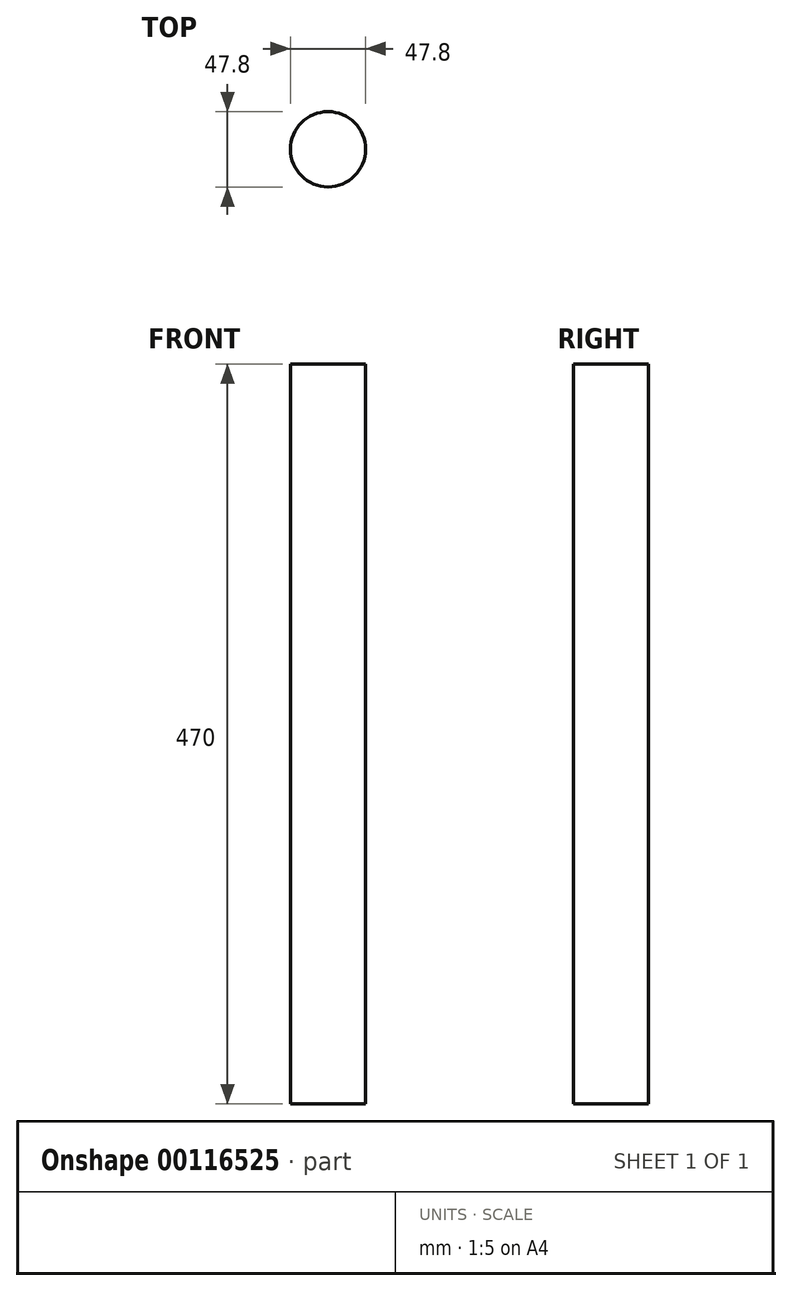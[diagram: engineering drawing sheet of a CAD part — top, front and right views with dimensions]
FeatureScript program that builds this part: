
annotation { "Feature Type Name" : "Feature", "Feature Type Description" : "" }
export const myFeature = defineFeature(function(context is Context, id is Id, definition is map)
    precondition{}
    {
        {
            var Q0;
            Q0=qCreatedBy(makeId("Top.planeOp"),FACE);
            var sketch = newSketch(context, id + "F0", { "sketchPlane" : qUnion([Q0])});
            skCircle(sketch, "E0", {"center": v(0, 0) * mm, "radius": 23.9 * mm});
            skSolve(sketch);
        }
        {
            var Q0;
            Q0=qSketchRegion(id+"F0",true);
            var Q1;
            Q1=makeQuery(id+"F0.imprint","IMPRINT",FACE,{"disambiguationData":[TD([[makeQuery(id+"F0.imprint","IMPRINT",EDGE,{"derivedFrom":sQuery(id+"F0.wireOp",EDGE,"E0")}),1.0]])]});
            extrude(context, id + "F1", {"entities" : qUnion([Q0, Q1]), "depth" : 470 * mm});
        }
    });
